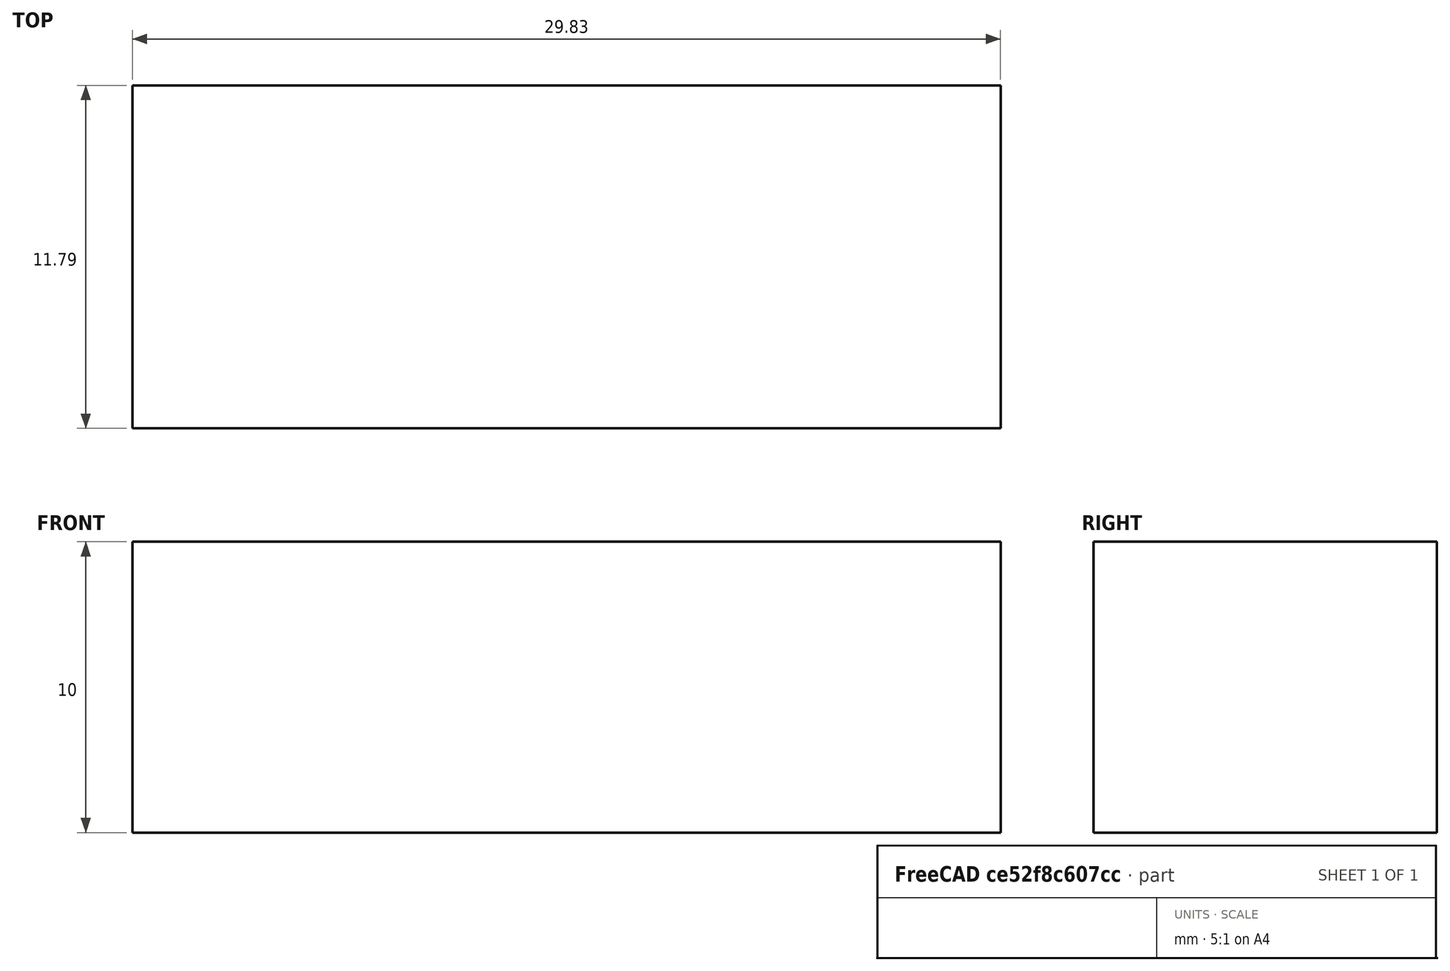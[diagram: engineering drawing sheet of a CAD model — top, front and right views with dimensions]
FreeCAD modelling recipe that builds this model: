
FCSTD DOCUMENT  (FreeCAD 0.19R16699 (Git))
Label: MasterPart
License: All rights reserved
LicenseURL: http://en.wikipedia.org/wiki/All_rights_reserved
objects: Sketcher::SketchObject×1, PartDesign::Pad×1, PartDesign::Body×1, App::Part×1
note: 4 computed .brp shape members not serialized (recipe doc carries the construction recipe); baked Part::Feature solids carry a one-line shape summary decoded from their .brp

FEATURE [Sketcher::SketchObject] Sketch  label="MasterSketch"
  MapMode = 5
  Support = -> [XY_Plane001]
  sketch-geometry (4):
    g0: LineSegment StartX=-12.5681 StartY=5.18184 StartZ=0 EndX=17.2633 EndY=5.18184 EndZ=0
    g1: LineSegment StartX=17.2633 StartY=5.18184 StartZ=0 EndX=17.2633 EndY=-6.61329 EndZ=0
    g2: LineSegment StartX=17.2633 StartY=-6.61329 StartZ=0 EndX=-12.5681 EndY=-6.61329 EndZ=0
    g3: LineSegment StartX=-12.5681 StartY=-6.61329 StartZ=0 EndX=-12.5681 EndY=5.18184 EndZ=0
  constraints (8):
    c: Coincident(g0,g1)
    c: Coincident(g1,g2)
    c: Coincident(g2,g3)
    c: Coincident(g3,g0)
    c: Horizontal(g0)
    c: Horizontal(g2)
    c: Vertical(g1)
    c: Vertical(g3)
FEATURE [PartDesign::Pad] Pad
  Length = 10
  Length2 = 100
  Profile = -> Sketch
  Type = 0
FEATURE [PartDesign::Body] Body  label="MasterBody"
  Group = -> [Sketch,Pad]
  Origin = -> Origin001
  Tip = -> Pad
FEATURE [App::Part] Part  label="MasterPart"
  Group = -> [Body]
  Origin = -> Origin
